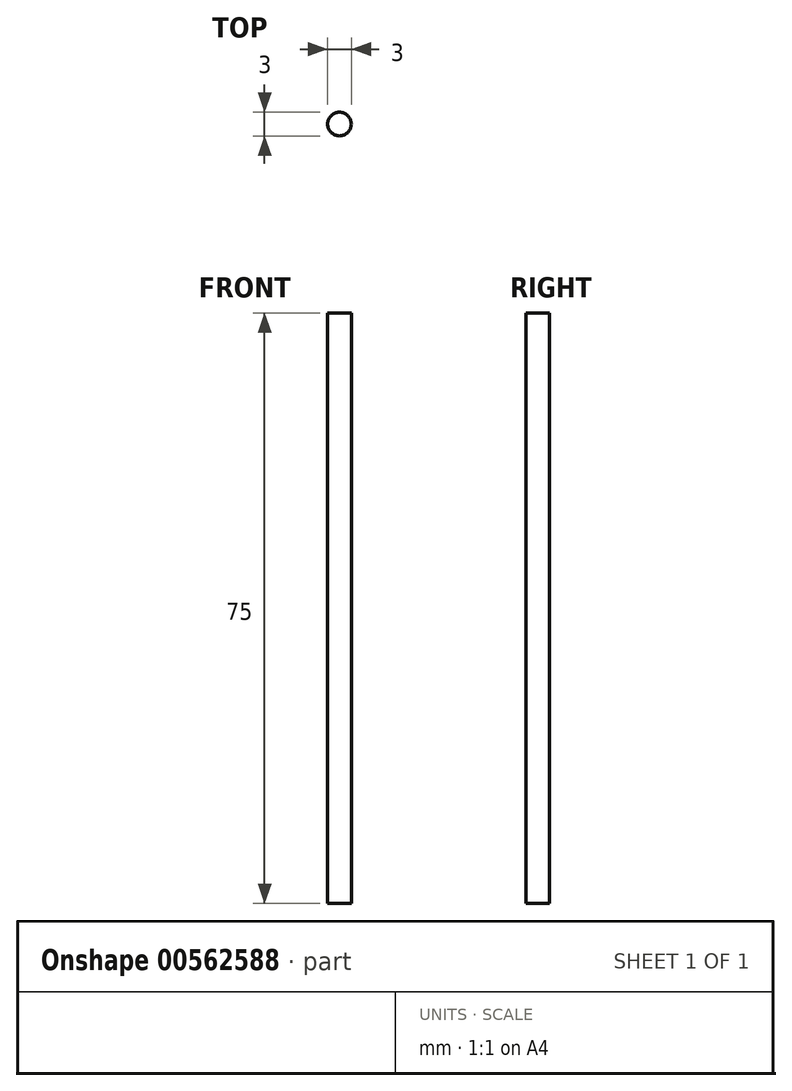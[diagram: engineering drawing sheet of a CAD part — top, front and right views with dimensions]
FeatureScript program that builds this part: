
annotation { "Feature Type Name" : "Feature", "Feature Type Description" : "" }
export const myFeature = defineFeature(function(context is Context, id is Id, definition is map)
    precondition{}
    {
        {
            var Q0;
            Q0=qCreatedBy(makeId("Top.planeOp"),FACE);
            var sketch = newSketch(context, id + "F0", { "sketchPlane" : qUnion([Q0])});
            skCircle(sketch, "E0", {"center": v(0, 0) * mm, "radius": 1.5 * mm});
            skSolve(sketch);
        }
        {
            var Q0;
            Q0 = qSketchRegion(id + "F0", true);
            extrude(context, id + "F1", {"entities" : qUnion([Q0]), "depth" : 75 * mm, "offsetDistance" : 25 * mm});
        }
    });
